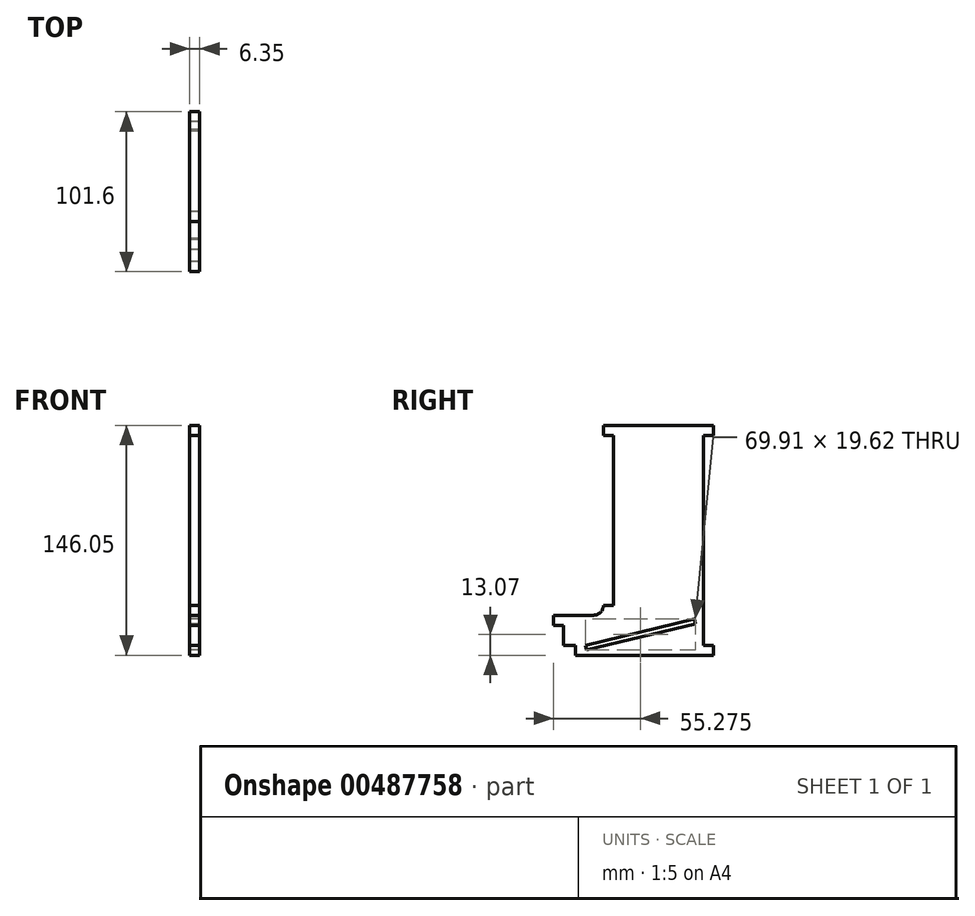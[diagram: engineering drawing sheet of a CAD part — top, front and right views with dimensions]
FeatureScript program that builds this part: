
annotation { "Feature Type Name" : "Feature", "Feature Type Description" : "" }
export const myFeature = defineFeature(function(context is Context, id is Id, definition is map)
    precondition{}
    {
        {
            var Q0;
            Q0=qCreatedBy(makeId("Right.planeOp"),FACE);
            var sketch = newSketch(context, id + "F0", { "sketchPlane" : qUnion([Q0])});
            skLineSegment(sketch, "E0.bottom", {"start": v(0, 0) * mm, "end": v(-69.85, 0) * mm});
            skLineSegment(sketch, "E0.top", {"start": v(0, 146.05) * mm, "end": v(-69.85, 146.05) * mm});
            skLineSegment(sketch, "E0.left", {"start": v(0, 0) * mm, "end": v(0, 146.05) * mm});
            skLineSegment(sketch, "E0.right", {"start": v(-69.85, 0) * mm, "end": v(-69.85, 146.05) * mm});
            skLineSegment(sketch, "E1.bottom", {"start": v(-69.85, 0) * mm, "end": v(-101.6, 0) * mm});
            skLineSegment(sketch, "E1.top", {"start": v(-69.85, 25.4) * mm, "end": v(-101.6, 25.4) * mm});
            skLineSegment(sketch, "E1.left", {"start": v(-69.85, 0) * mm, "end": v(-69.85, 25.4) * mm});
            skLineSegment(sketch, "E1.right", {"start": v(-101.6, 0) * mm, "end": v(-101.6, 25.4) * mm});
            skSolve(sketch);
        }
        {
            var Q0;
            Q0=qSketchRegion(id+"F0",true);
            extrude(context, id + "F1", {"entities" : qUnion([Q0]), "depth" : 6.35 * mm});
        }
        {
            var Q0;
            Q0=qCreatedBy(makeId("Right.planeOp"),FACE);
            var sketch = newSketch(context, id + "F2", { "sketchPlane" : qUnion([Q0])});
            skLineSegment(sketch, "E2.bottom", {"start": v(0, 6.35) * mm, "end": v(-6.35, 6.35) * mm});
            skLineSegment(sketch, "E2.top", {"start": v(0, 139.7) * mm, "end": v(-6.35, 139.7) * mm});
            skLineSegment(sketch, "E2.left", {"start": v(0, 6.35) * mm, "end": v(0, 139.7) * mm});
            skLineSegment(sketch, "E2.right", {"start": v(-6.35, 6.35) * mm, "end": v(-6.35, 139.7) * mm});
            skSolve(sketch);
        }
        {
            var Q0;
            Q0=qSketchRegion(id+"F2",true);
            extrude(context, id + "F3", {"entities" : qUnion([Q0]), "operationType" : NewBodyOperationType.REMOVE, "depth" : 12.45 * mm});
        }
        {
            var Q0;
            Q0=qCreatedBy(makeId("Right.planeOp"),FACE);
            var sketch = newSketch(context, id + "F4", { "sketchPlane" : qUnion([Q0])});
            skLineSegment(sketch, "E3.bottom", {"start": v(-63.5, 139.7) * mm, "end": v(-69.85, 139.7) * mm});
            skLineSegment(sketch, "E3.top", {"start": v(-63.5, 31.75) * mm, "end": v(-69.85, 31.75) * mm});
            skLineSegment(sketch, "E3.left", {"start": v(-63.5, 139.7) * mm, "end": v(-63.5, 31.75) * mm});
            skLineSegment(sketch, "E3.right", {"start": v(-69.85, 139.7) * mm, "end": v(-69.85, 31.75) * mm});
            skPoint(sketch, "E3.middle", {"position": v(-66.68, 85.73) * mm});
            skSolve(sketch);
        }
        {
            var Q0;
            Q0=qSketchRegion(id+"F4",true);
            extrude(context, id + "F5", {"entities" : qUnion([Q0]), "operationType" : NewBodyOperationType.REMOVE, "depth" : 9.9 * mm});
        }
        {
            var Q0;
            Q0=qCreatedBy(makeId("Right.planeOp"),FACE);
            var sketch = newSketch(context, id + "F6", { "sketchPlane" : qUnion([Q0])});
            skLineSegment(sketch, "E4.bottom", {"start": v(-101.6, 19.05) * mm, "end": v(-95.25, 19.05) * mm});
            skLineSegment(sketch, "E4.top", {"start": v(-101.6, 0) * mm, "end": v(-95.25, 0) * mm});
            skLineSegment(sketch, "E4.left", {"start": v(-101.6, 19.05) * mm, "end": v(-101.6, 0) * mm});
            skLineSegment(sketch, "E4.right", {"start": v(-95.25, 19.05) * mm, "end": v(-95.25, 0) * mm});
            skLineSegment(sketch, "E5.bottom", {"start": v(-87.63, 6.35) * mm, "end": v(-95.25, 6.35) * mm});
            skLineSegment(sketch, "E5.top", {"start": v(-87.63, 0) * mm, "end": v(-95.25, 0) * mm});
            skLineSegment(sketch, "E5.left", {"start": v(-87.63, 6.35) * mm, "end": v(-87.63, 0) * mm});
            skLineSegment(sketch, "E5.right", {"start": v(-95.25, 6.35) * mm, "end": v(-95.25, 0) * mm});
            skPoint(sketch, "E5.middle", {"position": v(-91.44, 3.18) * mm});
            skSolve(sketch);
        }
        {
            var Q0;
            Q0=qSketchRegion(id+"F6",true);
            extrude(context, id + "F7", {"entities" : qUnion([Q0]), "operationType" : NewBodyOperationType.REMOVE, "depth" : 10.67 * mm});
        }
        {
            var Q0;
            Q0=qCreatedBy(makeId("Right.planeOp"),FACE);
            var sketch = newSketch(context, id + "F8", { "sketchPlane" : qUnion([Q0])});
            skLineSegment(sketch, "E6.bottom", {"start": v(-69.85, 25.4) * mm, "end": v(-76.2, 25.4) * mm});
            skLineSegment(sketch, "E6.top", {"start": v(-69.85, 31.75) * mm, "end": v(-76.2, 31.75) * mm});
            skLineSegment(sketch, "E6.left", {"start": v(-69.85, 25.4) * mm, "end": v(-69.85, 31.75) * mm});
            skLineSegment(sketch, "E6.right", {"start": v(-76.2, 25.4) * mm, "end": v(-76.2, 31.75) * mm});
            skSolve(sketch);
        }
        {
            var Q0;
            Q0=qSketchRegion(id+"F8",true);
            extrude(context, id + "F9", {"entities" : qUnion([Q0]), "operationType" : NewBodyOperationType.ADD, "depth" : 6.35 * mm});
        }
        {
            var Q0;
            Q0=qCreatedBy(makeId("Right.planeOp"),FACE);
            var sketch = newSketch(context, id + "F10", { "sketchPlane" : qUnion([Q0])});
            skCircle(sketch, "E7", {"center": v(-76.2, 31.75) * mm, "radius": 6.35 * mm});
            skSolve(sketch);
        }
        {
            var Q0;
            Q0=qSketchRegion(id+"F10",true);
            extrude(context, id + "F11", {"entities" : qUnion([Q0]), "operationType" : NewBodyOperationType.REMOVE, "depth" : 8.94 * mm});
        }
        {
            var Q0;
            Q0=makeQuery(id+"F9.boolean.opBoolean","MERGE",FACE,{"derivedFrom":[makeQuery(id+"F1.opExtrude","CAP_FACE",FACE,{"disambiguationData":[OSD([sQuery(id+"F0.wireOp",EDGE,"E0.bottom"),sQuery(id+"F0.wireOp",EDGE,"E0.top"),sQuery(id+"F0.wireOp",EDGE,"E0.left"),sQuery(id+"F0.wireOp",EDGE,"E0.right"),sQuery(id+"F0.wireOp",EDGE,"E1.bottom"),sQuery(id+"F0.wireOp",EDGE,"E1.top"),sQuery(id+"F0.wireOp",EDGE,"E1.right")])],"isStart":true}),makeQuery(id+"F9.opExtrude","CAP_FACE",FACE,{"disambiguationData":[OSD([sQuery(id+"F8.wireOp",EDGE,"E6.bottom"),sQuery(id+"F8.wireOp",EDGE,"E6.top"),sQuery(id+"F8.wireOp",EDGE,"E6.left"),sQuery(id+"F8.wireOp",EDGE,"E6.right")])],"isStart":true})]});
            var sketch = newSketch(context, id + "F12", { "sketchPlane" : qUnion([Q0])});
            skLineSegment(sketch, "E8", {"start": v(81.28, 6.35) * mm, "end": v(12.1, 22.88) * mm});
            skLineSegment(sketch, "E9", {"start": v(12.1, 22.88) * mm, "end": v(11.37, 19.8) * mm});
            skLineSegment(sketch, "E10", {"start": v(11.37, 19.8) * mm, "end": v(80.54, 3.26) * mm});
            skLineSegment(sketch, "E11", {"start": v(80.54, 3.26) * mm, "end": v(81.28, 6.35) * mm});
            skSolve(sketch);
        }
        {
            var Q0;
            Q0=qSketchRegion(id+"F12",true);
            extrude(context, id + "F13", {"entities" : qUnion([Q0]), "operationType" : NewBodyOperationType.REMOVE, "endBound" : BoundingType.THROUGH_ALL, "oppositeDirection" : true, "depth" : 25.4 * mm});
        }
    });
